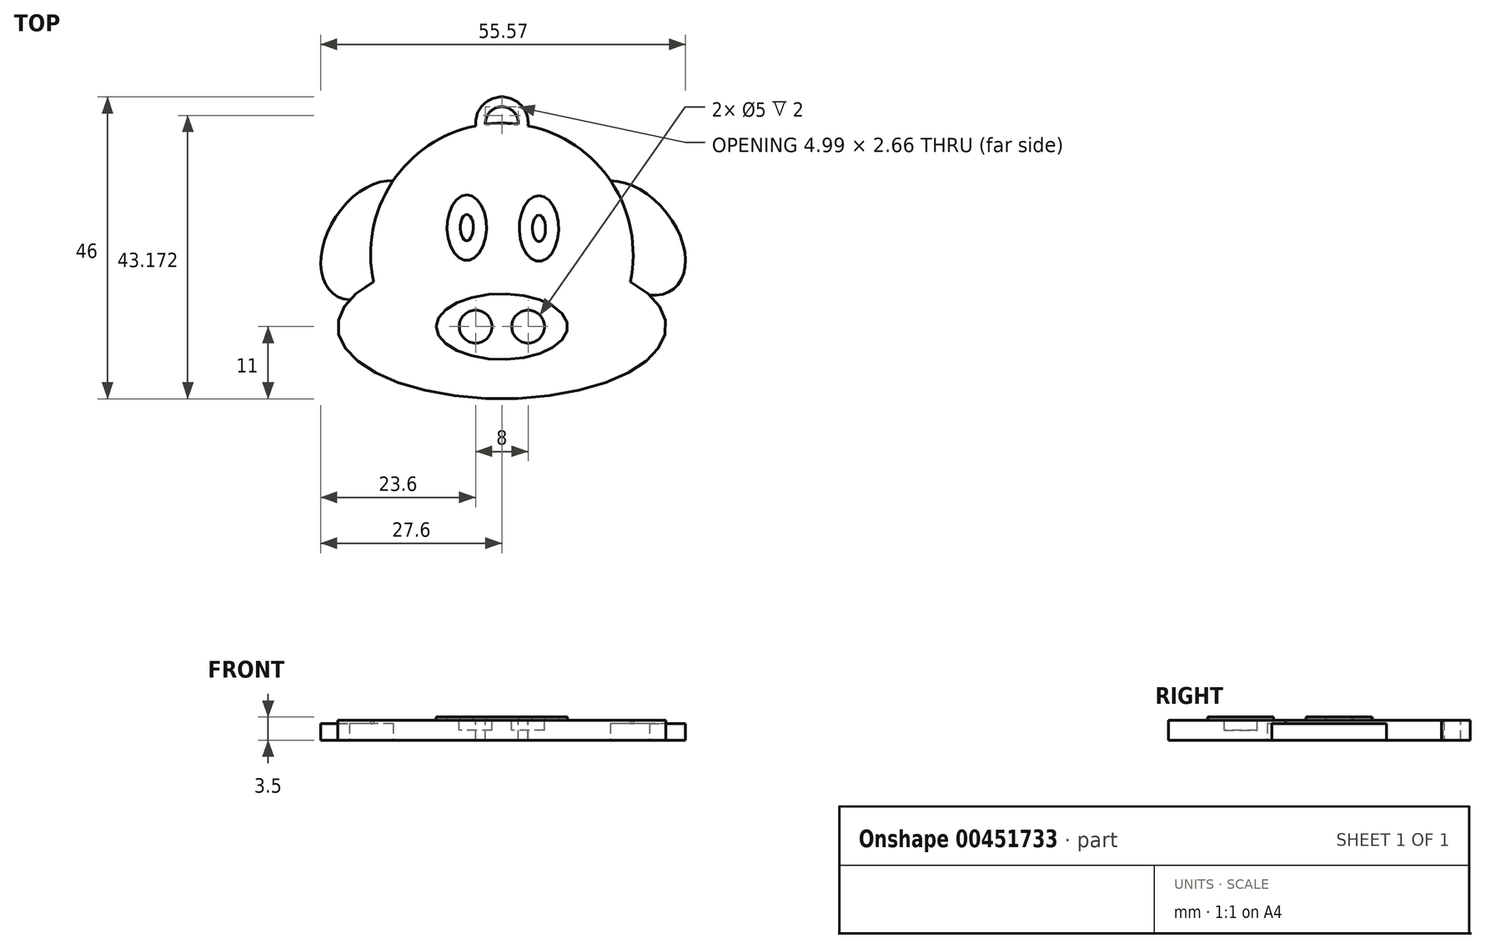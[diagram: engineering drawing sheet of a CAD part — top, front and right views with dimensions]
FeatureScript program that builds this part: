
annotation { "Feature Type Name" : "Feature", "Feature Type Description" : "" }
export const myFeature = defineFeature(function(context is Context, id is Id, definition is map)
    precondition{}
    {
        {
            var Q0;
            Q0=qCreatedBy(makeId("Top.planeOp"),FACE);
            var sketch = newSketch(context, id + "F0", { "sketchPlane" : qUnion([Q0])});
            skEllipticalArc(sketch, "E0", {});
            skArc(sketch, "E1", {"start": v(19.56, 6.85) * mm, "mid": v(0, 31) * mm, "end": v(-19.56, 6.85) * mm});
            skEllipticalArc(sketch, "E2", {});
            skEllipticalArc(sketch, "E3", {});
            skEllipse(sketch, "E4", {"center": v(0, 0) * mm, "majorRadius": 10 * mm, "minorRadius": 5 * mm, "majorAxis": v(-1, 0)});
            const initialGuessF0  = {"E0": [0, 0, -1, 0, 0.025, 0.011, 5.611176050648764, 3.813601910120616], "E2": [0.01984313483298443, 0.0135, -0.642429846310491, 0.7663444999277279, 0.01, 0.0065, 2.56242571486681, 5.7888265158144705], "E3": [-0.019884557693906457, 0.013145778487567029, 0.546078189586536, 0.8377342125387335, 0.01, 0.0065, 0.3398741252794217, 3.479694823237764]};
            skSetInitialGuess(sketch, initialGuessF0);
            skSolve(sketch);
        }
        {
            var Q0;
            Q0=qCreatedBy(makeId("Top.planeOp"),FACE);
            var sketch = newSketch(context, id + "F1", { "sketchPlane" : qUnion([Q0])});
            skEllipse(sketch, "E5", {"center": v(5.65, 14.97) * mm, "majorRadius": 5 * mm, "minorRadius": 3 * mm, "majorAxis": v(0, 1)});
            skEllipse(sketch, "E6", {"center": v(-5.35, 15.08) * mm, "majorRadius": 5 * mm, "minorRadius": 3 * mm, "majorAxis": v(0, 1)});
            skEllipse(sketch, "E7", {"center": v(-5.35, 15.08) * mm, "majorRadius": 2 * mm, "minorRadius": 1 * mm, "majorAxis": v(0, 1)});
            skEllipse(sketch, "E8", {"center": v(5.65, 14.97) * mm, "majorRadius": 2 * mm, "minorRadius": 1 * mm, "majorAxis": v(0, 1)});
            skSolve(sketch);
        }
        {
            var Q0;
            Q0=makeQuery(id+"F0.imprint","IMPRINT",FACE,{"disambiguationData":[TD([[makeQuery(id+"F0.imprint","IMPRINT",EDGE,{"derivedFrom":sQuery(id+"F0.wireOp",EDGE,"E4")}),-1.0]])]});
            extrude(context, id + "F2", {"entities" : qUnion([Q0]), "depth" : 3 * mm});
        }
        {
            var Q0;
            Q0 = qSketchRegion(id + "F1", true);
            extrude(context, id + "F3", {"entities" : qUnion([Q0]), "operationType" : NewBodyOperationType.ADD, "depth" : 3.5 * mm});
        }
        {
            var Q0;
            {var subQ0=sQuery(id+"F0.wireOp",EDGE,"E2");Q0=makeQuery(id+"F0.imprint","IMPRINT",FACE,{"disambiguationData":[TD([[makeQuery(id+"F0.imprint","IMPRINT",EDGE,{"derivedFrom":subQ0}),1.0]])]});}
            var Q1;
            {var subQ3=sQuery(id+"F0.wireOp",EDGE,"E3");Q1=makeQuery(id+"F0.imprint","IMPRINT",FACE,{"disambiguationData":[TD([[makeQuery(id+"F0.imprint","IMPRINT",EDGE,{"derivedFrom":subQ3}),1.0]])]});}
            extrude(context, id + "F4", {"entities" : qUnion([Q0, Q1]), "operationType" : NewBodyOperationType.ADD, "depth" : 2.5 * mm});
        }
        {
            var Q0;
            Q0=qCreatedBy(makeId("Top.planeOp"),FACE);
            var sketch = newSketch(context, id + "F5", { "sketchPlane" : qUnion([Q0])});
            skEllipse(sketch, "E9", {"center": v(0, 0) * mm, "majorRadius": 10 * mm, "minorRadius": 5 * mm, "majorAxis": v(-1, 0)});
            skSolve(sketch);
        }
        {
            var Q0;
            Q0 = qSketchRegion(id + "F5", true);
            extrude(context, id + "F6", {"entities" : qUnion([Q0]), "operationType" : NewBodyOperationType.ADD, "depth" : 3.5 * mm});
        }
        {
            var Q0;
            Q0=makeQuery(id+"F1.imprint","IMPRINT",FACE,{"disambiguationData":[TD([[makeQuery(id+"F1.imprint","IMPRINT",EDGE,{"derivedFrom":sQuery(id+"F1.wireOp",EDGE,"E5")}),1.0]])]});
            var Q1;
            Q1=makeQuery(id+"F1.imprint","IMPRINT",FACE,{"disambiguationData":[TD([[makeQuery(id+"F1.imprint","IMPRINT",EDGE,{"derivedFrom":sQuery(id+"F1.wireOp",EDGE,"E6")}),1.0]])]});
            var Q2;
            Q2=sQuery(id+"F0.wireOp",EDGE,"3TFyB5rS-D3O6-SwbQ-6BoB-0NFnf7UDGUmk");
            var Q3;
            Q3=sQuery(id+"F0.wireOp",EDGE,"uzdhvJss-yJEM-cYmP-aWyf-DT077lo6DGaH");
            extrude(context, id + "F7", {"entities" : qUnion([Q0, Q1]), "operationType" : NewBodyOperationType.ADD, "surfaceEntities" : qUnion([Q2, Q3]), "depth" : 1 * mm});
        }
        {
            var Q0;
            Q0=makeQuery(id+"F6.opExtrude","CAP_FACE",FACE,{"disambiguationData":[OSD([sQuery(id+"F5.wireOp",EDGE,"E9")])],"isStart":false});
            var sketch = newSketch(context, id + "F8", { "sketchPlane" : qUnion([Q0])});
            skCircle(sketch, "E10", {"center": v(-4, 0) * mm, "radius": 2.5 * mm});
            skCircle(sketch, "E11", {"center": v(4, 0) * mm, "radius": 2.5 * mm});
            skSolve(sketch);
        }
        {
            var Q0;
            Q0=makeQuery(id+"F8.imprint","IMPRINT",FACE,{"disambiguationData":[TD([[makeQuery(id+"F8.imprint","IMPRINT",EDGE,{"derivedFrom":sQuery(id+"F8.wireOp",EDGE,"E10")}),1.0]])]});
            var Q1;
            Q1=makeQuery(id+"F8.imprint","IMPRINT",FACE,{"disambiguationData":[TD([[makeQuery(id+"F8.imprint","IMPRINT",EDGE,{"derivedFrom":sQuery(id+"F8.wireOp",EDGE,"E11")}),1.0]])]});
            var Q2;
            Q2=sQuery(id+"F8.wireOp",EDGE,"E10");
            var Q3;
            Q3=sQuery(id+"F8.wireOp",EDGE,"E11");
            extrude(context, id + "F9", {"entities" : qUnion([Q0, Q1]), "operationType" : NewBodyOperationType.REMOVE, "surfaceEntities" : qUnion([Q2, Q3]), "oppositeDirection" : true, "depth" : 2 * mm});
        }
        {
            var Q0;
            {var subQ0=sQuery(id+"F0.wireOp",EDGE,"E4");var subQ1=sQuery(id+"F0.wireOp",EDGE,"E1");var subQ2=sQuery(id+"F0.wireOp",EDGE,"E0");Q0=makeQuery(id+"F3.boolean.opBoolean","SPLIT",FACE,{"disambiguationData":[TD([makeQuery(id+"F2.opExtrude","SWEPT_FACE",FACE,{"disambiguationData":[OSD([subQ2])]})])],"derivedFrom":makeQuery(id+"F2.opExtrude","CAP_FACE",FACE,{"disambiguationData":[OSD([subQ2,subQ1,subQ0])],"isStart":false})});}
            var sketch = newSketch(context, id + "F10", { "sketchPlane" : qUnion([Q0])});
            skArc(sketch, "E12", {"start": v(2.5, 30.84) * mm, "mid": v(0, 33.5) * mm, "end": v(-2.5, 30.84) * mm});
            skArc(sketch, "E13", {"start": v(3.98, 30.6) * mm, "mid": v(0, 35) * mm, "end": v(-3.98, 30.6) * mm});
            skSolve(sketch);
        }
        {
            var Q0;
            {var subQ0=sQuery(id+"F10.wireOp",EDGE,"E12");Q0=makeQuery(id+"F10.imprint","IMPRINT",FACE,{"disambiguationData":[TD([[makeQuery(id+"F10.imprint","IMPRINT",EDGE,{"derivedFrom":subQ0}),-1.0]])]});}
            extrude(context, id + "F11", {"entities" : qUnion([Q0]), "operationType" : NewBodyOperationType.ADD, "oppositeDirection" : true, "depth" : 3 * mm});
        }
    });
